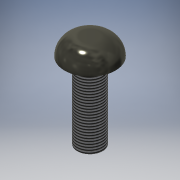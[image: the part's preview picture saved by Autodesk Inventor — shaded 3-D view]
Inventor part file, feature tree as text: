
AUTODESK INVENTOR PART (.ipt)
format: ipt  version: 2016 (Build 200138000, 138)  size: 145,408 bytes
history: native  units: mm
features: extrude x3, sketch x3, other x1, fillet x1, thread x1
ambient origin geometry x1: Origin
bodies: Body1 (feature_tree)
feature tree (9):
  other  "ソリッド1"
  extrude  "押し出し1"  Depth=5.0mm
  extrude  "押し出し2"  Depth=6.0mm TaperAngle=0.0deg
  fillet  "フィレット1"  Radius=10.0mm
  thread  "ねじ1"
  extrude  "押し出し3"  Depth=3.4mm TaperAngle=0.0deg
  sketch  "スケッチ1"
  sketch  "スケッチ2"
  sketch  "スケッチ3"
